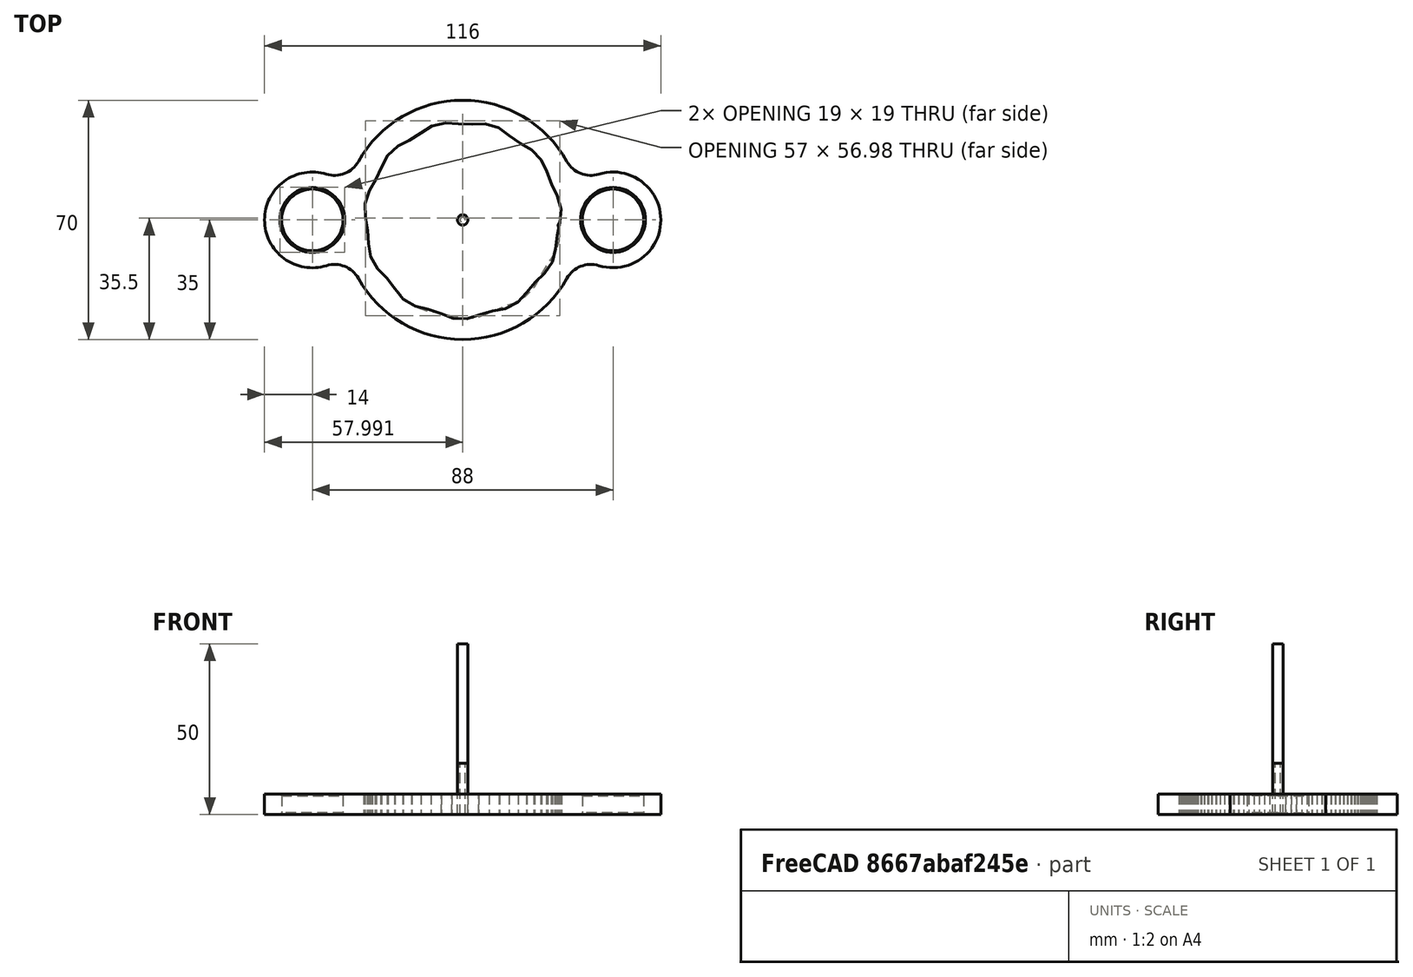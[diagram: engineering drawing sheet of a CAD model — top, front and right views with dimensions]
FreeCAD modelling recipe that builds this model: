
FCSTD DOCUMENT  (FreeCAD 0.20R29603 (Git))
Label: Out_gear_pin
License: All rights reserved
LicenseURL: http://en.wikipedia.org/wiki/All_rights_reserved
objects: Part::FeaturePython×4, Path::FeaturePython×4, App::DocumentObjectGroup×3, Part::Feature×1, App::FeaturePython×1
note: 6 computed .brp shape members not serialized (recipe doc carries the construction recipe); baked Part::Feature solids carry a one-line shape summary decoded from their .brp

FEATURE [Part::Feature] Part__Feature  label="@·.721512.002"
  shape: bbox 116 x 70 x 6 mm, 25 faces (baked)
FEATURE [App::FeaturePython] SetupSheet  # Path/CAM operation (typed FeaturePython)
  ClearanceHeightExpression = OpStockZMax+SetupSheet.ClearanceHeightOffset
  ClearanceHeightOffset = 5
  CoolantMode = 0
  CoolantModes = None | Flood | Mist
  FinalDepthExpression = OpFinalDepth
  HorizRapid = 3.33333
  SafeHeightExpression = OpStockZMax+SetupSheet.SafeHeightOffset
  SafeHeightOffset = 3
  StartDepthExpression = OpStartDepth
  StepDownExpression = OpToolDiameter
  VertRapid = 1.66667
FEATURE [Part::FeaturePython] Clone  label="Model-@·.721512.002"  # Draft clone (typed FeaturePython)
  AttacherType = Attacher::AttachEngine3D
  Fuse = false
  Objects = -> [Part__Feature]
  PathResource = Model
  Placement = pos=(0,0,-7.1e-15) rot=(0,-1,0;3.14159rad)
  Scale = (1,1,1)
FEATURE [App::DocumentObjectGroup] Model
  Group = -> [Clone]
FEATURE [Part::FeaturePython] ToolBit  label="1.5mm Endmill"  # Path/CAM toolbit (typed FeaturePython)
  BitPropertyNames = Chipload | CuttingEdgeHeight | Diameter | Flutes | Length | Material | ShankDiameter | SpindleDirection
  BitShape = <path>
  Chipload = 0
  CuttingEdgeHeight = 15
  Diameter = 1.5
  File = <path>
  Flutes = 0
  Length = 50
  Material = 0
  ShankDiameter = 3
  ShapeName = endmill
  SpindleDirection = 0
FEATURE [Path::FeaturePython] __5mm_Endmill  label="1.5mm Endmill001"  # Path/CAM operation (typed FeaturePython)
  HorizFeed = 3.33333
  HorizRapid = 3.33333
  SpindleDir = 0
  SpindleSpeed = 0
  Tool = -> ToolBit
  ToolNumber = 3
  VertFeed = 1.66667
  VertRapid = 1.66667
  expr: HorizRapid = SetupSheet.HorizRapid
  expr: VertRapid = SetupSheet.VertRapid
FEATURE [Path::FeaturePython] Profile  # Path/CAM operation (typed FeaturePython)
  Active = true
  AreaParams:
    Tolerance = 1e-07
    FitArcs = True
    Simplify = False
    CleanDistance = 0.0
    Accuracy = 0.01
    Unit = 1.0
    MinArcPoints = 4
    MaxArcPoints = 100
    ClipperScale = 10000000.0
    Fill = 0
    Coplanar = 0
    Reorient = True
    Outline = False
    Explode = False
    OpenMode = 0
    Deflection = 0.01
    SubjectFill = 0
    ClipFill = 0
    Offset = -0.75
    ExtraPass = 0
    Stepover = 0.0
    LastStepover = 0.0
    JoinType = 0
    EndType = 0
    MiterLimit = 2.0
    RoundPrecision = 0.0
    PocketMode = 0
    ToolRadius = 1.0
    PocketExtraOffset = 0.0
    PocketStepover = 0.0
    PocketLastStepover = 0.0
    FromCenter = False
    Angle = 45.0
    AngleShift = 0.0
    Shift = 0.0
    Thicken = False
    SectionCount = -1
    Stepdown = 1.0
    SectionOffset = 0.0
    SectionTolerance = 1e-06
    SectionMode = 2
    Project = False
  Base = -> [Clone]
  ClearanceHeight = 11
  CoolantMode = 0
  CycleTime = 00:04:08
  Direction = 0
  FinalDepth = -6
  HandleMultipleFeatures = 0
  JoinType = 0
  MiterLimit = 0.1
  OffsetExtra = 0
  OpFinalDepth = 0
  OpStartDepth = 6
  OpStockZMax = 6
  OpStockZMin = 0
  OpToolDiameter = 1.5
  PathParams = {'orientation': 1, 'feedrate': 3.3333333333333335, 'feedrate_v': 1.6666666666666667, 'verbose': True, 'resume_height': 9.0, 'retraction': 11.0, 'return_end': True, 'preamble': False}
  SafeHeight = 9
  Side = 1
  SplitArcs = false
  StartDepth = 0
  StartPoint = (0,0,0)
  StepDown = 1.5
  ToolController = -> __5mm_Endmill
  UseComp = true
  UseStartPoint = false
  processCircles = false
  processHoles = false
  processPerimeter = true
  expr: ClearanceHeight = OpStockZMax + SetupSheet.ClearanceHeightOffset
  expr: FinalDepth = -6 mm
  expr: SafeHeight = OpStockZMax + SetupSheet.SafeHeightOffset
  expr: StartDepth = 0
  expr: StepDown = OpToolDiameter
FEATURE [App::DocumentObjectGroup] Operations
  Group = -> [Profile]
FEATURE [Part::FeaturePython] ToolBit001  label="3mm Endmill"  # Path/CAM toolbit (typed FeaturePython)
  BitPropertyNames = Chipload | CuttingEdgeHeight | Diameter | Flutes | Length | Material | ShankDiameter | SpindleDirection
  BitShape = <path>
  Chipload = 0
  CuttingEdgeHeight = 15
  Diameter = 3
  File = <path>
  Flutes = 0
  Length = 50
  Material = 0
  ShankDiameter = 3
  ShapeName = endmill
  SpindleDirection = 0
FEATURE [Path::FeaturePython] _mm_Endmill  label="3mm Endmill001"  # Path/CAM operation (typed FeaturePython)
  HorizFeed = 0
  HorizRapid = 3.33333
  SpindleDir = 0
  SpindleSpeed = 0
  Tool = -> ToolBit001
  ToolNumber = 4
  VertFeed = 0
  VertRapid = 1.66667
  expr: HorizRapid = SetupSheet.HorizRapid
  expr: VertRapid = SetupSheet.VertRapid
FEATURE [App::DocumentObjectGroup] Tools
  Group = -> [__5mm_Endmill,_mm_Endmill]
FEATURE [Part::FeaturePython] Clone056  label="Stock-@·.721512.002"  # Draft clone (typed FeaturePython)
  AttacherType = Attacher::AttachEngine3D
  Fuse = false
  Objects = -> [Part__Feature]
  PathResource = Stock
  Scale = (1,1,1)
  StockType = Unknown
FEATURE [Path::FeaturePython] Job  # Path/CAM operation (typed FeaturePython)
  CycleTime = 00:04:08
  Fixtures = G54
  GeometryTolerance = 0.01
  JobType = 0
  LastPostProcessDate = 2023-08-25 11:30:50.261987
  LastPostProcessOutput = <path>
  Model = -> Model
  Operations = -> Operations
  OrderOutputBy = 0
  PostProcessor = 8
  PostProcessorArgs = --bcnc
  PostProcessorOutputFile = <path>
  SetupSheet = -> SetupSheet
  SplitOutput = false
  Stock = -> Clone056
  Tools = -> Tools
note: 6 file-system paths scrubbed to <path> (originals preserved in the JSON sidecar)
